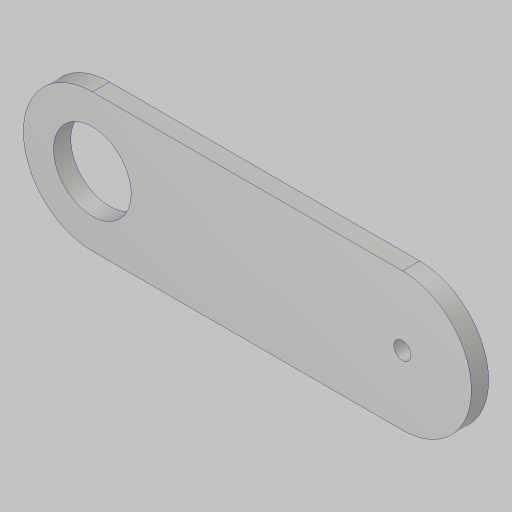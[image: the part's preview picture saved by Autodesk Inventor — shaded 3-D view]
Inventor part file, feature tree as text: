
AUTODESK INVENTOR PART (.ipt)
format: ipt  version: 2023.5 (Build 275446000, 446)  size: 108,544 bytes
history: native  units: in
note: dims shown in document units (in); Inventor stores cm internally (conversion verified against a paired STEP export)
features: extrude x1, sketch x1
ambient origin geometry x8: Origin, YZ Plane, XZ Plane, XY Plane, X Axis, Y Axis, Z Axis, Center Point
bodies: Solid1 (feature_tree)
feature tree (2):
  extrude  "Extrusion1"  Depth=0.25in
  sketch  "Sketch1"  dims[d0=1.125in d1=0.25in d2=2.0in d3=4.5in d4=0.25in d5=0.0in]
